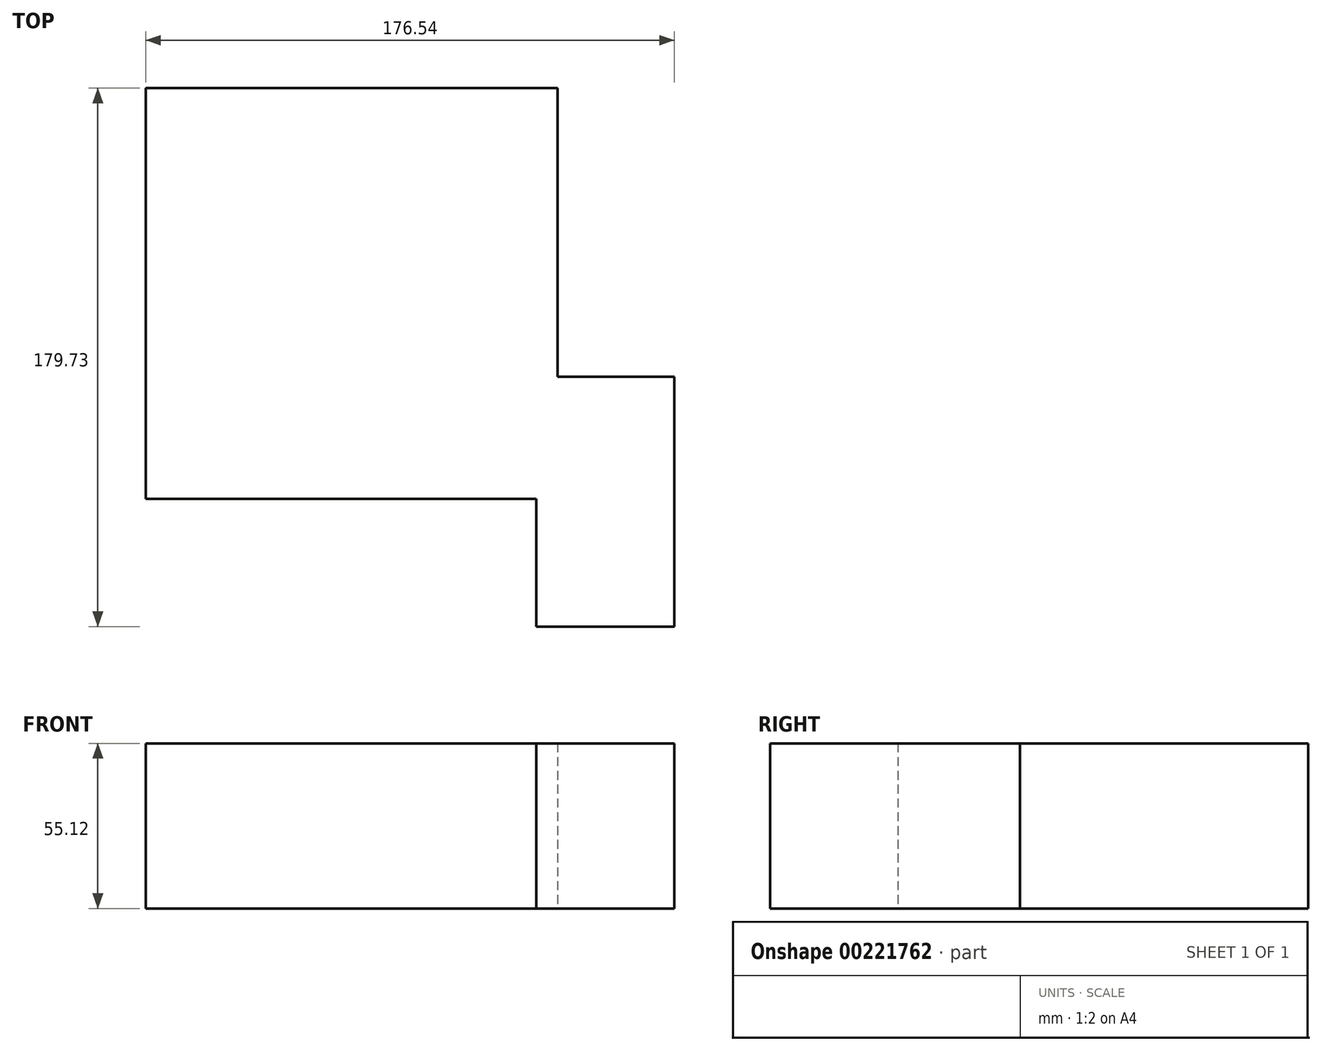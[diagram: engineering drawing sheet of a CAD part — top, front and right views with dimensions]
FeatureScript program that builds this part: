
annotation { "Feature Type Name" : "Feature", "Feature Type Description" : "" }
export const myFeature = defineFeature(function(context is Context, id is Id, definition is map)
    precondition{}
    {
        {
            var Q0;
            Q0=qCreatedBy(makeId("Top.planeOp"),FACE);
            var sketch = newSketch(context, id + "F0", { "sketchPlane" : qUnion([Q0])});
            skLineSegment(sketch, "E0", {"start": v(-72.03, -71.62) * mm, "end": v(-72.03, 65.47) * mm});
            skLineSegment(sketch, "E1", {"start": v(-72.03, 65.47) * mm, "end": v(65.5, 65.47) * mm});
            skLineSegment(sketch, "E2", {"start": v(65.5, 65.47) * mm, "end": v(65.5, -30.85) * mm});
            skLineSegment(sketch, "E3", {"start": v(65.5, -30.85) * mm, "end": v(104.5, -30.85) * mm});
            skLineSegment(sketch, "E4", {"start": v(104.5, -30.85) * mm, "end": v(104.5, -114.26) * mm});
            skLineSegment(sketch, "E5", {"start": v(104.5, -114.26) * mm, "end": v(58.45, -114.26) * mm});
            skLineSegment(sketch, "E6", {"start": v(58.45, -114.26) * mm, "end": v(58.45, -71.62) * mm});
            skLineSegment(sketch, "E7", {"start": v(58.45, -71.62) * mm, "end": v(-72.03, -71.62) * mm});
            skSolve(sketch);
        }
        {
            var Q0;
            Q0 = qSketchRegion(id + "F0", true);
            extrude(context, id + "F1", {"entities" : qUnion([Q0]), "depth" : 55.12 * mm});
        }
        {
            var Q0;
            Q0=qCreatedBy(makeId("Right.planeOp"),FACE);
            cPlane(context, id + "F2", {"entities" : qUnion([Q0]), "cplaneType" : CPlaneType.OFFSET, "offset" : 25.4 * mm, "width" : 152.4 * mm, "height" : 152.4 * mm});
        }
    });
